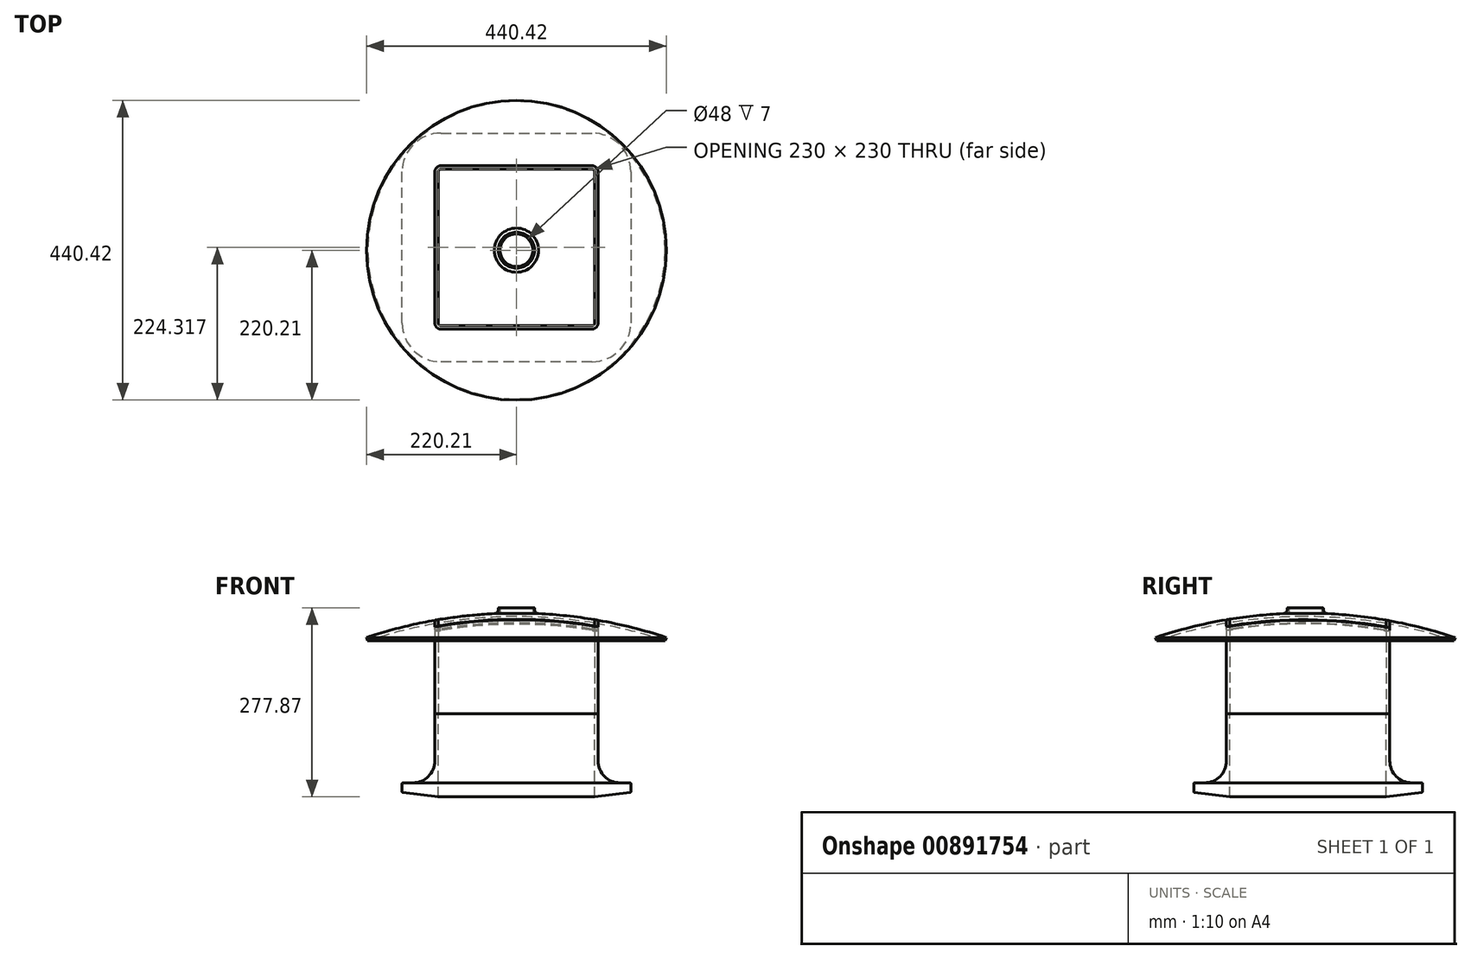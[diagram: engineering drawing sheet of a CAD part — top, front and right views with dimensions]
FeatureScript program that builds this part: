
annotation { "Feature Type Name" : "Feature", "Feature Type Description" : "" }
export const myFeature = defineFeature(function(context is Context, id is Id, definition is map)
    precondition{}
    {
        {
            var Q0;
            Q0=qCreatedBy(makeId("Top.planeOp"),FACE);
            var sketch = newSketch(context, id + "F0", { "sketchPlane" : qUnion([Q0])});
            skLineSegment(sketch, "E0.bottom", {"start": v(-111, 119.1) * mm, "end": v(111, 119.1) * mm});
            skLineSegment(sketch, "E0.top", {"start": v(-111, -110.9) * mm, "end": v(111, -110.9) * mm});
            skLineSegment(sketch, "E0.left", {"start": v(-115, 115.1) * mm, "end": v(-115, -106.9) * mm});
            skLineSegment(sketch, "E0.right", {"start": v(115, 115.1) * mm, "end": v(115, -106.9) * mm});
            skPoint(sketch, "E0.middle", {"position": v(0, 4.1) * mm});
            skPoint(sketch, "E1.visualSharp", {"position": v(-115, -110.9) * mm});
            skArc(sketch, "E1.filletArc", {"start": v(-115, -106.9) * mm, "mid": v(-113.83, -109.72) * mm, "end": v(-111, -110.9) * mm});
            skPoint(sketch, "E2.visualSharp", {"position": v(-115, 119.1) * mm});
            skArc(sketch, "E2.filletArc", {"start": v(-111, 119.1) * mm, "mid": v(-113.83, 117.94) * mm, "end": v(-115, 115.1) * mm});
            skPoint(sketch, "E3.visualSharp", {"position": v(115, 119.1) * mm});
            skArc(sketch, "E3.filletArc", {"start": v(115, 115.1) * mm, "mid": v(113.83, 117.94) * mm, "end": v(111, 119.1) * mm});
            skPoint(sketch, "E4.visualSharp", {"position": v(115, -110.9) * mm});
            skArc(sketch, "E4.filletArc", {"start": v(111, -110.9) * mm, "mid": v(113.83, -109.72) * mm, "end": v(115, -106.9) * mm});
            skSolve(sketch);
        }
        {
            var Q0;
            Q0=qCreatedBy(makeId("Front.planeOp"),FACE);
            var sketch = newSketch(context, id + "F1", { "sketchPlane" : qUnion([Q0])});
            skLineSegment(sketch, "E5.0.0", {"start": v(-115, 0) * mm, "end": v(-111, 0) * mm});
            skLineSegment(sketch, "E5.0.1", {"start": v(-111, 0) * mm, "end": v(111, 0) * mm});
            skLineSegment(sketch, "E5.0.2", {"start": v(111, 0) * mm, "end": v(115, 0) * mm});
            skLineSegment(sketch, "E5.0.4", {"start": v(115, 0) * mm, "end": v(111, 0) * mm});
            skLineSegment(sketch, "E5.0.5", {"start": v(111, 0) * mm, "end": v(-111, 0) * mm});
            skLineSegment(sketch, "E5.0.6", {"start": v(-111, 0) * mm, "end": v(-115, 0) * mm});
            skLineSegment(sketch, "E6", {"start": v(115, 0) * mm, "end": v(115, 230) * mm, "construction": true});
            skLineSegment(sketch, "E7", {"start": v(168, -5.56) * mm, "end": v(168, -8.56) * mm});
            skLineSegment(sketch, "E8", {"start": v(168, -8.56) * mm, "end": v(115, -8.56) * mm});
            skLineSegment(sketch, "E9", {"start": v(115, -8.56) * mm, "end": v(115, 0) * mm});
            skLineSegment(sketch, "E10", {"start": v(152, -4.56) * mm, "end": v(167, -4.56) * mm});
            skArc(sketch, "E11.filletArc", {"start": v(120, 27.44) * mm, "mid": v(129.37, 4.82) * mm, "end": v(152, -4.56) * mm});
            skPoint(sketch, "E12.visualSharp", {"position": v(168, -4.56) * mm});
            skArc(sketch, "E12.filletArc", {"start": v(168, -5.56) * mm, "mid": v(167.7, -4.85) * mm, "end": v(167, -4.56) * mm});
            skLineSegment(sketch, "E13", {"start": v(168, -8.56) * mm, "end": v(168, -17.67) * mm});
            skLineSegment(sketch, "E14", {"start": v(167.12, -18.67) * mm, "end": v(144, -21.57) * mm});
            skLineSegment(sketch, "E15", {"start": v(144, -21.57) * mm, "end": v(115, -25.22) * mm});
            skLineSegment(sketch, "E16", {"start": v(115, -25.22) * mm, "end": v(115, -8.56) * mm});
            skPoint(sketch, "E17.visualSharp", {"position": v(168, -18.56) * mm});
            skArc(sketch, "E17.filletArc", {"start": v(167.12, -18.67) * mm, "mid": v(167.75, -18.33) * mm, "end": v(168, -17.67) * mm});
            skLineSegment(sketch, "E18", {"start": v(0, 0) * mm, "end": v(0, 230) * mm, "construction": true});
            skLineSegment(sketch, "E19", {"start": v(-115, 0) * mm, "end": v(-115, 230) * mm, "construction": true});
            skLineSegment(sketch, "E20", {"start": v(120, 27.44) * mm, "end": v(120, 97.05) * mm});
            skLineSegment(sketch, "E21", {"start": v(120, 97.05) * mm, "end": v(115, 97.05) * mm});
            skLineSegment(sketch, "E22", {"start": v(115, 97.05) * mm, "end": v(115, 0) * mm});
            skLineSegment(sketch, "E23", {"start": v(120, 97.05) * mm, "end": v(120, 288.6) * mm, "construction": true});
            skLineSegment(sketch, "E24", {"start": v(115, 230) * mm, "end": v(120, 230) * mm});
            skLineSegment(sketch, "E25", {"start": v(120, 230) * mm, "end": v(120, 234.3) * mm});
            skLineSegment(sketch, "E26", {"start": v(0, 0) * mm, "end": v(0, -2176.27) * mm, "construction": true});
            skLineSegment(sketch, "E27", {"start": v(-115, 230) * mm, "end": v(0, -450.35) * mm, "construction": true});
            skLineSegment(sketch, "E28", {"start": v(0, 230) * mm, "end": v(0, 347.41) * mm, "construction": true});
            skArc(sketch, "E29", {"start": v(0, 239.65) * mm, "mid": v(-110.75, 230.7) * mm, "end": v(-218.63, 204.1) * mm});
            skArc(sketch, "E30", {"start": v(0, 244.65) * mm, "mid": v(-198.4, 215.73) * mm, "end": v(-380.3, 131.37) * mm});
            skLineSegment(sketch, "E31", {"start": v(0, -450.35) * mm, "end": v(-218.63, 204.1) * mm, "construction": true});
            skLineSegment(sketch, "E32", {"start": v(-218.63, 204.1) * mm, "end": v(-220.2, 208.84) * mm});
            skLineSegment(sketch, "E33", {"start": v(0, 244.65) * mm, "end": v(0, 239.65) * mm});
            skLineSegment(sketch, "E34", {"start": v(0, 244.65) * mm, "end": v(-24, 244.65) * mm});
            skLineSegment(sketch, "E35", {"start": v(-24, 244.65) * mm, "end": v(-24, 244.24) * mm});
            skLineSegment(sketch, "E36", {"start": v(-24, 244.65) * mm, "end": v(-24, 251.65) * mm});
            skLineSegment(sketch, "E37", {"start": v(-25, 252.65) * mm, "end": v(-25.5, 252.65) * mm});
            skLineSegment(sketch, "E38", {"start": v(-26.5, 251.65) * mm, "end": v(-26.5, 250.65) * mm});
            skLineSegment(sketch, "E39", {"start": v(-26.5, 250.65) * mm, "end": v(-32.5, 250.65) * mm, "construction": true});
            skLineSegment(sketch, "E40", {"start": v(-32.5, 250.65) * mm, "end": v(-32.5, 243.9) * mm, "construction": true});
            skArc(sketch, "E41", {"start": v(-26.5, 250.65) * mm, "mid": v(-28.22, 246.13) * mm, "end": v(-32.5, 243.9) * mm});
            skPoint(sketch, "E42.visualSharp", {"position": v(-26.5, 252.65) * mm});
            skArc(sketch, "E42.filletArc", {"start": v(-25.5, 252.65) * mm, "mid": v(-26.2, 252.36) * mm, "end": v(-26.5, 251.65) * mm});
            skPoint(sketch, "E43.visualSharp", {"position": v(-24, 252.65) * mm});
            skArc(sketch, "E43.filletArc", {"start": v(-24, 251.65) * mm, "mid": v(-24.3, 252.36) * mm, "end": v(-25, 252.65) * mm});
            skSolve(sketch);
        }
        {
            var Q0;
            Q0=makeQuery(id+"F1.imprint","IMPRINT",FACE,{"disambiguationData":[TD([[makeQuery(id+"F1.imprint","IMPRINT",EDGE,{"derivedFrom":sQuery(id+"F1.wireOp",EDGE,"E6")}),-1.0]])]});
            var Q1;
            Q1=makeQuery(id+"F1.imprint","IMPRINT",FACE,{"disambiguationData":[TD([[makeQuery(id+"F1.imprint","IMPRINT",EDGE,{"derivedFrom":sQuery(id+"F1.wireOp",EDGE,"E8")}),1.0]])]});
            var Q2;
            Q2=makeQuery(id+"F1.imprint","IMPRINT",FACE,{"disambiguationData":[TD([[makeQuery(id+"F1.imprint","IMPRINT",EDGE,{"derivedFrom":sQuery(id+"F1.wireOp",EDGE,"E7")}),-1.0]])]});
            var Q3;
            Q3=sQuery(id+"F0.wireOp",EDGE,"E0.right");
            var Q4;
            Q4=sQuery(id+"F0.wireOp",EDGE,"E3.filletArc");
            var Q5;
            Q5=sQuery(id+"F0.wireOp",EDGE,"E0.bottom");
            var Q6;
            Q6=sQuery(id+"F0.wireOp",EDGE,"E2.filletArc");
            var Q7;
            Q7=sQuery(id+"F0.wireOp",EDGE,"E0.left");
            var Q8;
            Q8=sQuery(id+"F0.wireOp",EDGE,"E1.filletArc");
            var Q9;
            Q9=sQuery(id+"F0.wireOp",EDGE,"E0.top");
            var Q10;
            Q10=sQuery(id+"F0.wireOp",EDGE,"E4.filletArc");
            sweep(context, id + "F2", {"profiles" : qUnion([Q0, Q1, Q2]), "path" : qUnion([Q3, Q4, Q5, Q6, Q7, Q8, Q9, Q10])});
        }
        {
            var Q0;
            Q0=makeQuery(id+"F1.imprint","IMPRINT",FACE,{"disambiguationData":[TD([[makeQuery(id+"F1.imprint","IMPRINT",EDGE,{"derivedFrom":sQuery(id+"F1.wireOp",EDGE,"E29")}),-1.0]])]});
            var Q1;
            {var subQ0=sQuery(id+"F1.wireOp",EDGE,"E35");Q1=makeQuery(id+"F1.imprint","IMPRINT",FACE,{"disambiguationData":[TD([[makeQuery(id+"F1.imprint","IMPRINT",EDGE,{"derivedFrom":subQ0}),-1.0]])]});}
            var Q2;
            {var subQ0=sQuery(id+"F1.wireOp",EDGE,"E34");Q2=makeQuery(id+"F1.imprint","IMPRINT",FACE,{"disambiguationData":[TD([[makeQuery(id+"F1.imprint","IMPRINT",EDGE,{"derivedFrom":subQ0}),1.0]])]});}
            var Q3;
            Q3=sQuery(id+"F1.wireOp",EDGE,"E18");
            revolve(context, id + "F3", {"surfaceOperationType" : NewSurfaceOperationType.NEW, "entities" : qUnion([Q0, Q1, Q2]), "axis" : qUnion([Q3]), "revolveType" : RevolveType.FULL});
        }
        {
            var Q0;
            Q0=makeQuery(id+"F2.opSweep","SWEPT_FACE",FACE,{"disambiguationData":[OSD([sQuery(id+"F0.wireOp",EDGE,"E0.right"),sQuery(id+"F1.wireOp",EDGE,"E21")])]});
            extrude(context, id + "F4", {"entities" : qUnion([Q0]), "operationType" : NewBodyOperationType.REMOVE, "depth" : 200 * mm, "offsetDistance" : 25 * mm});
        }
        {
            var Q0;
            Q0=makeQuery(id+"F2.opSweep","SWEPT_FACE",FACE,{"disambiguationData":[OSD([sQuery(id+"F0.wireOp",EDGE,"E0.right"),sQuery(id+"F1.wireOp",EDGE,"E21")])]});
            var Q1;
            Q1=makeQuery(id+"F4.boolean.opBoolean","SPLIT",FACE,{"disambiguationData":[TD([makeQuery(id+"F3.opRevolve","SWEPT_FACE",FACE,{"disambiguationData":[OSD([sQuery(id+"F1.wireOp",EDGE,"E41")])]})])],"derivedFrom":makeQuery(id+"F3.opRevolve","SWEPT_FACE",FACE,{"disambiguationData":[OSD([sQuery(id+"F1.wireOp",EDGE,"E30")])]})});
            extrude(context, id + "F5", {"entities" : qUnion([Q0]), "endBound" : BoundingType.UP_TO_SURFACE, "depth" : 25 * mm, "endBoundEntityFace" : qUnion([Q1]), "offsetDistance" : 25 * mm});
        }
    });
